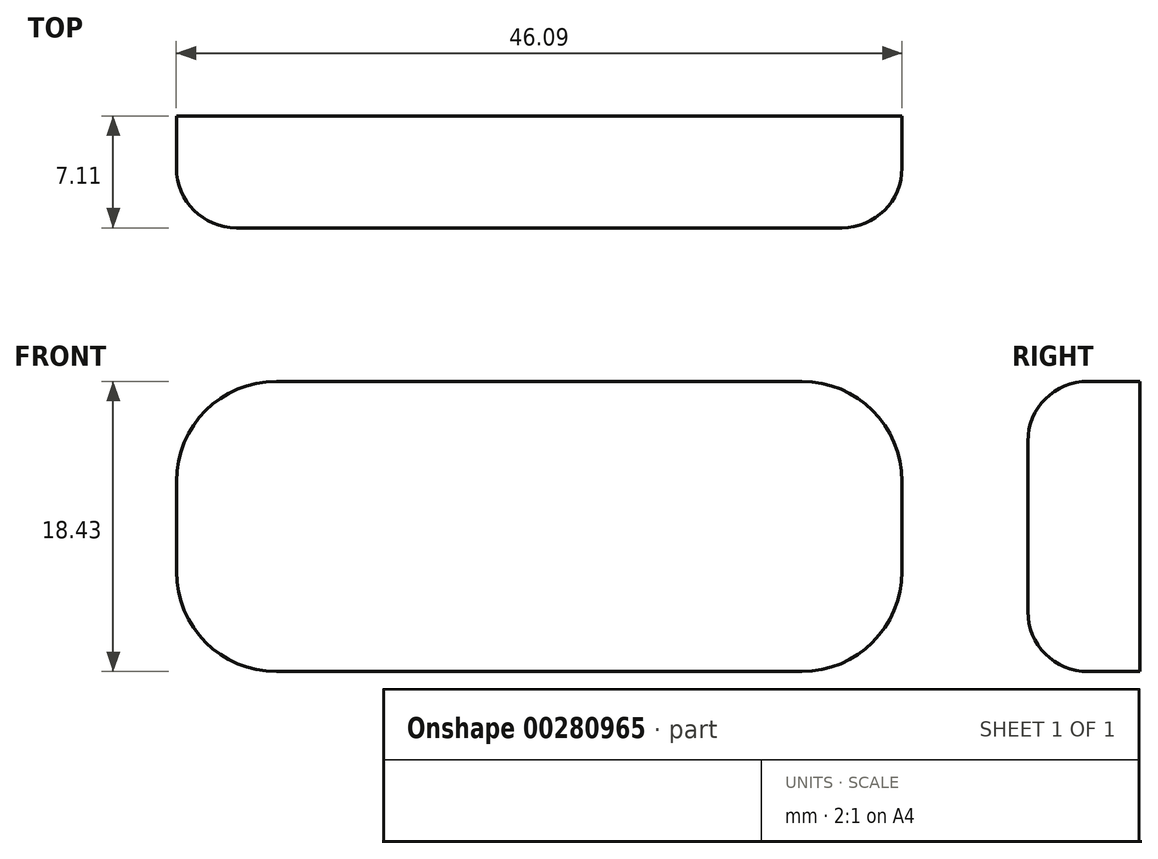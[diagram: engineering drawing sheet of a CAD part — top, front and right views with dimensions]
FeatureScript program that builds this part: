
annotation { "Feature Type Name" : "Feature", "Feature Type Description" : "" }
export const myFeature = defineFeature(function(context is Context, id is Id, definition is map)
    precondition{}
    {
        {
            var Q0;
            Q0=qCreatedBy(makeId("Front.planeOp"),FACE);
            var sketch = newSketch(context, id + "F0", { "sketchPlane" : qUnion([Q0])});
            skLineSegment(sketch, "E0.bottom", {"start": v(-53.16, 41.11) * mm, "end": v(-19.77, 41.11) * mm});
            skLineSegment(sketch, "E0.top", {"start": v(-53.16, 22.68) * mm, "end": v(-19.77, 22.68) * mm});
            skLineSegment(sketch, "E0.left", {"start": v(-59.5, 34.76) * mm, "end": v(-59.5, 29.03) * mm});
            skLineSegment(sketch, "E0.right", {"start": v(-13.42, 34.76) * mm, "end": v(-13.42, 29.03) * mm});
            skPoint(sketch, "E1.visualSharp", {"position": v(-59.5, 41.11) * mm});
            skArc(sketch, "E1.filletArc", {"start": v(-53.16, 41.11) * mm, "mid": v(-57.65, 39.25) * mm, "end": v(-59.5, 34.76) * mm});
            skPoint(sketch, "E2.visualSharp", {"position": v(-13.42, 41.11) * mm});
            skArc(sketch, "E2.filletArc", {"start": v(-13.42, 34.76) * mm, "mid": v(-15.28, 39.25) * mm, "end": v(-19.77, 41.11) * mm});
            skPoint(sketch, "E3.visualSharp", {"position": v(-13.42, 22.68) * mm});
            skArc(sketch, "E3.filletArc", {"start": v(-19.77, 22.68) * mm, "mid": v(-15.28, 24.54) * mm, "end": v(-13.42, 29.03) * mm});
            skPoint(sketch, "E4.visualSharp", {"position": v(-59.5, 22.68) * mm});
            skArc(sketch, "E4.filletArc", {"start": v(-59.5, 29.03) * mm, "mid": v(-57.65, 24.54) * mm, "end": v(-53.16, 22.68) * mm});
            skSolve(sketch);
        }
        {
            var Q0;
            Q0=makeQuery(id+"F0.imprint","IMPRINT",FACE,{"disambiguationData":[TD([[makeQuery(id+"F0.imprint","IMPRINT",EDGE,{"derivedFrom":sQuery(id+"F0.wireOp",EDGE,"E0.bottom")}),-1.0]])]});
            extrude(context, id + "F1", {"entities" : qUnion([Q0]), "depth" : 7.11 * mm});
        }
        {
            var Q0;
            Q0=makeQuery(id+"F1.opExtrude","CAP_FACE",FACE,{"disambiguationData":[OSD([sQuery(id+"F0.wireOp",EDGE,"E0.bottom"),sQuery(id+"F0.wireOp",EDGE,"E0.top"),sQuery(id+"F0.wireOp",EDGE,"E0.left"),sQuery(id+"F0.wireOp",EDGE,"E0.right"),sQuery(id+"F0.wireOp",EDGE,"E1.filletArc"),sQuery(id+"F0.wireOp",EDGE,"E2.filletArc"),sQuery(id+"F0.wireOp",EDGE,"E3.filletArc"),sQuery(id+"F0.wireOp",EDGE,"E4.filletArc")])],"isStart":false});
            fillet(context, id + "F2", {"entities" : qUnion([Q0]), "radius" : 3.8 * mm, "tangentPropagation" : true, "allowEdgeOverflow" : false});
        }
    });
